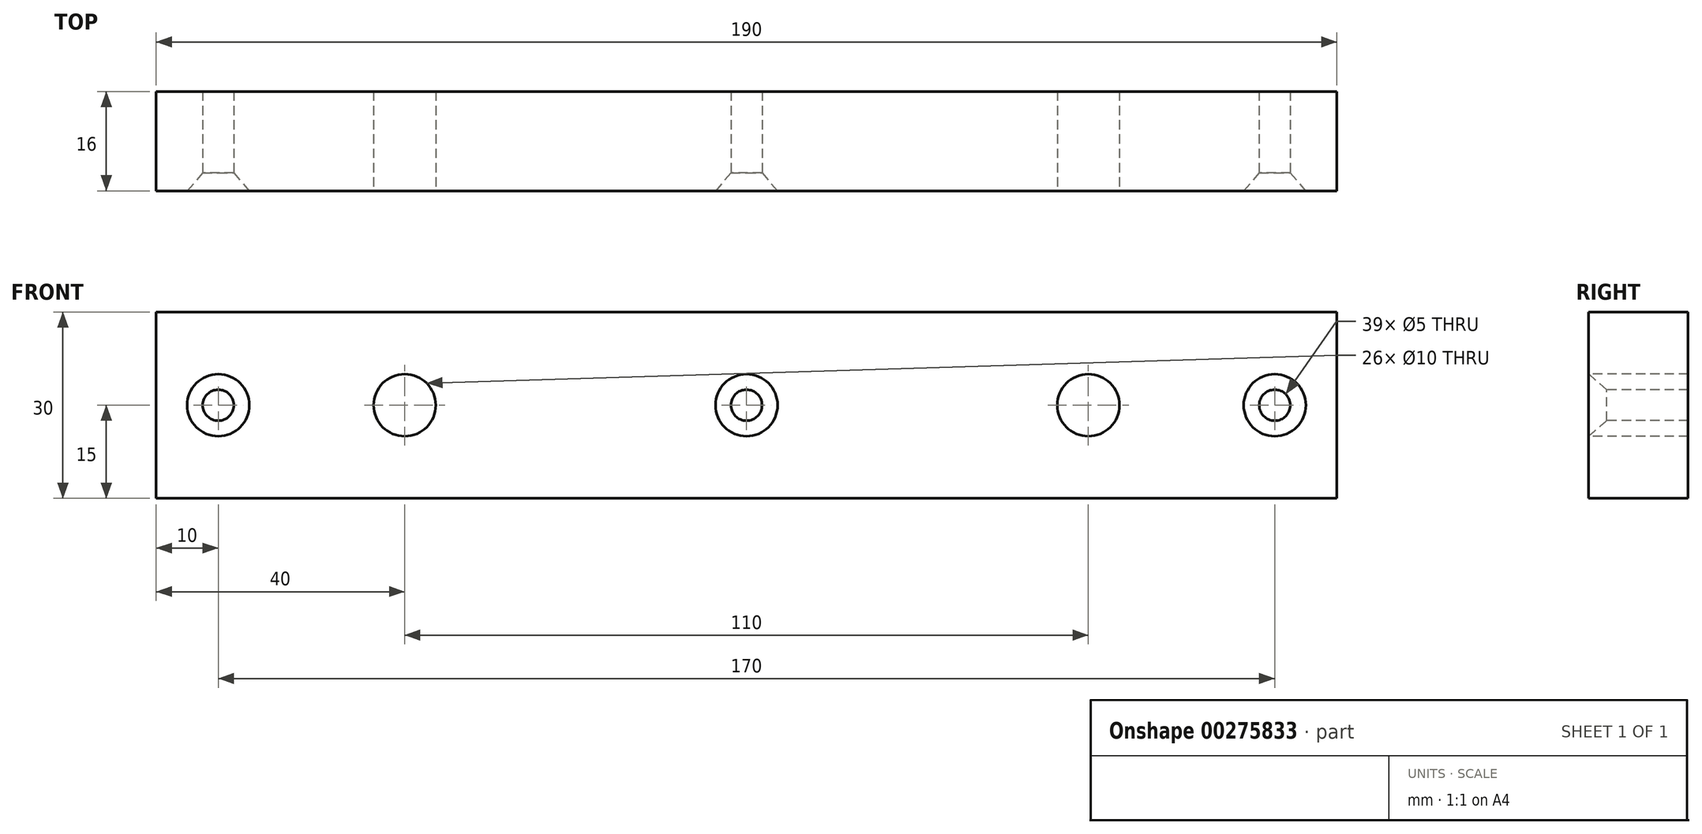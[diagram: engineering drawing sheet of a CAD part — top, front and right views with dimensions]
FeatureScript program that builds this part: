
annotation { "Feature Type Name" : "Feature", "Feature Type Description" : "" }
export const myFeature = defineFeature(function(context is Context, id is Id, definition is map)
    precondition{}
    {
        {
            var Q0;
            Q0=qCreatedBy(makeId("Front.planeOp"),FACE);
            var sketch = newSketch(context, id + "F0", { "sketchPlane" : qUnion([Q0])});
            skLineSegment(sketch, "E0.bottom", {"start": v(0, 0) * mm, "end": v(190, 0) * mm});
            skLineSegment(sketch, "E0.top", {"start": v(0, -30) * mm, "end": v(190, -30) * mm});
            skLineSegment(sketch, "E0.left", {"start": v(0, 0) * mm, "end": v(0, -30) * mm});
            skLineSegment(sketch, "E0.right", {"start": v(190, 0) * mm, "end": v(190, -30) * mm});
            skSolve(sketch);
        }
        {
            var Q0;
            Q0 = qSketchRegion(id + "F0", true);
            var Q1;
            Q1=makeQuery(id+"F0.imprint","IMPRINT",FACE,{"disambiguationData":[TD([[makeQuery(id+"F0.imprint","IMPRINT",EDGE,{"derivedFrom":sQuery(id+"F0.wireOp",EDGE,"E0.bottom")}),-1.0]])]});
            extrude(context, id + "F1", {"entities" : qUnion([Q0, Q1]), "depth" : 16 * mm});
        }
        {
            var Q0;
            Q0=makeQuery(id+"F1.opExtrude","CAP_FACE",FACE,{"disambiguationData":[OSD([sQuery(id+"F0.wireOp",EDGE,"E0.bottom"),sQuery(id+"F0.wireOp",EDGE,"E0.top"),sQuery(id+"F0.wireOp",EDGE,"E0.left"),sQuery(id+"F0.wireOp",EDGE,"E0.right")])],"isStart":false});
            var sketch = newSketch(context, id + "F2", { "sketchPlane" : qUnion([Q0])});
            skPoint(sketch, "E1", {"position": v(10, -15) * mm});
            skPoint(sketch, "E2", {"position": v(40, -15) * mm});
            skPoint(sketch, "E3", {"position": v(95, -15) * mm});
            skPoint(sketch, "E4", {"position": v(150, -15) * mm});
            skPoint(sketch, "E5", {"position": v(180, -15) * mm});
            skSolve(sketch);
        }
        {
            var Q0;
            Q0=sQuery(id+"F2.wireOp",VERTEX,"E2");
            var Q1;
            Q1=sQuery(id+"F2.wireOp",VERTEX,"E4");
            var Q2;
            Q2=makeQuery(id+"F1.opExtrude","SWEPT_BODY",BODY,{"disambiguationData":[OSD([sQuery(id+"F0.wireOp",EDGE,"E0.bottom"),sQuery(id+"F0.wireOp",EDGE,"E0.top"),sQuery(id+"F0.wireOp",EDGE,"E0.left"),sQuery(id+"F0.wireOp",EDGE,"E0.right")])]});
            hole(context, id + "F3", {"style" : HoleStyle.SIMPLE, "endStyle" : HoleEndStyle.THROUGH, "holeDiameter" : 10 * mm, "tappedDepth" : 50 * mm, "tapClearance" : 3, "locations" : qUnion([Q0, Q1]), "scope" : qUnion([Q2])});
        }
        {
            var Q0;
            Q0=sQuery(id+"F2.wireOp",VERTEX,"E1");
            var Q1;
            Q1=sQuery(id+"F2.wireOp",VERTEX,"E3");
            var Q2;
            Q2=sQuery(id+"F2.wireOp",VERTEX,"E5");
            var Q3;
            Q3=makeQuery(id+"F1.opExtrude","SWEPT_BODY",BODY,{"disambiguationData":[OSD([sQuery(id+"F0.wireOp",EDGE,"E0.bottom"),sQuery(id+"F0.wireOp",EDGE,"E0.top"),sQuery(id+"F0.wireOp",EDGE,"E0.left"),sQuery(id+"F0.wireOp",EDGE,"E0.right")])]});
            hole(context, id + "F4", {"style" : HoleStyle.C_SINK, "endStyle" : HoleEndStyle.THROUGH, "holeDiameter" : 5 * mm, "cSinkDiameter" : 10 * mm, "cSinkAngle" : 82 * degree, "tappedDepth" : 50 * mm, "tapClearance" : 3, "locations" : qUnion([Q0, Q1, Q2]), "scope" : qUnion([Q3])});
        }
    });
